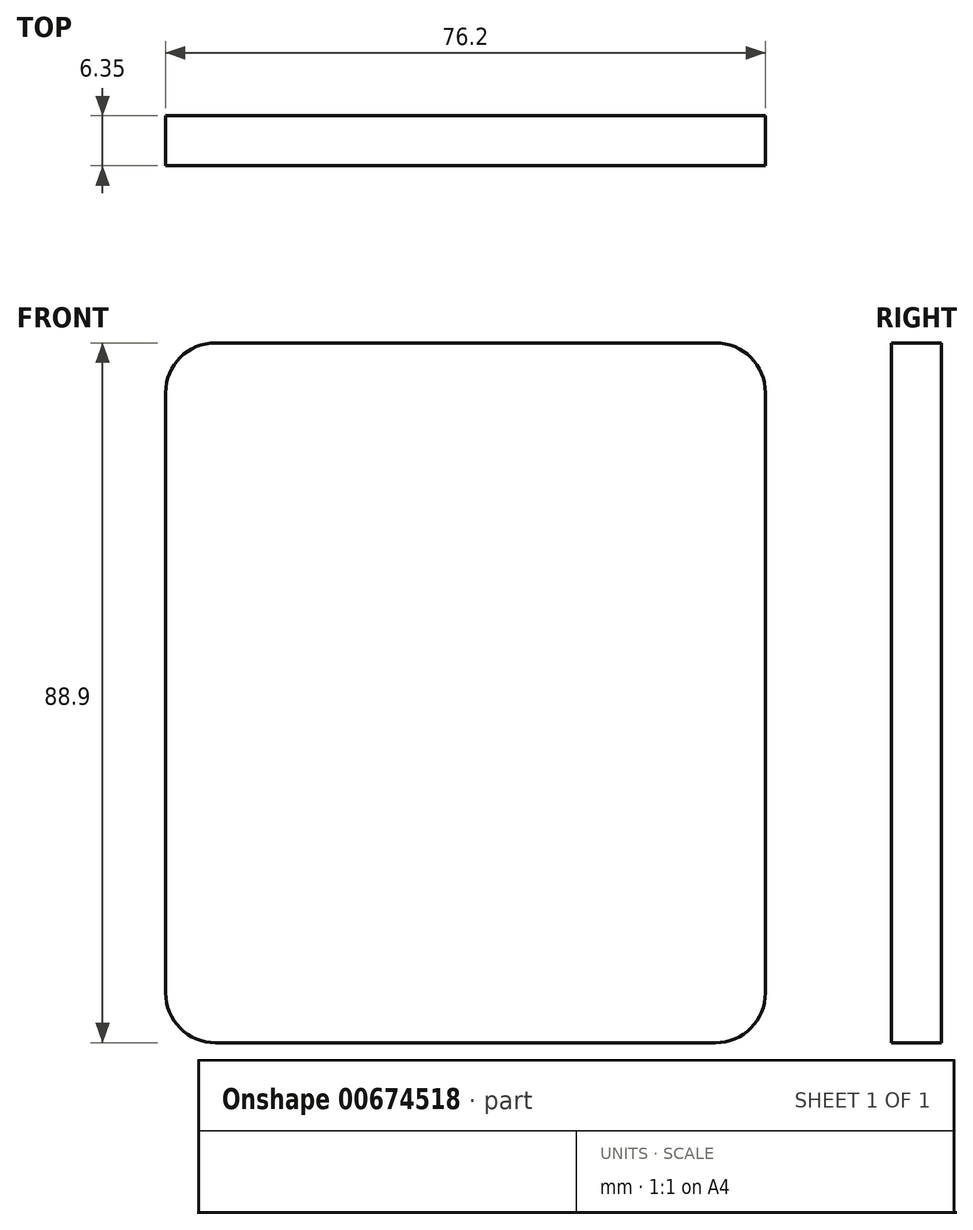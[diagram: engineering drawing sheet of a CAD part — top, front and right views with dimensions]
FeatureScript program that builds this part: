
annotation { "Feature Type Name" : "Feature", "Feature Type Description" : "" }
export const myFeature = defineFeature(function(context is Context, id is Id, definition is map)
    precondition{}
    {
        {
            var Q0;
            Q0=qCreatedBy(makeId("Front.planeOp"),FACE);
            var sketch = newSketch(context, id + "F0", { "sketchPlane" : qUnion([Q0])});
            skLineSegment(sketch, "E0.bottom", {"start": v(31.75, 44.45) * mm, "end": v(-31.75, 44.45) * mm});
            skLineSegment(sketch, "E0.top", {"start": v(31.75, -44.45) * mm, "end": v(-31.75, -44.45) * mm});
            skLineSegment(sketch, "E0.left", {"start": v(38.1, 38.1) * mm, "end": v(38.1, -38.1) * mm});
            skLineSegment(sketch, "E0.right", {"start": v(-38.1, 38.1) * mm, "end": v(-38.1, -38.1) * mm});
            skPoint(sketch, "E0.middle", {"position": v(0, 0) * mm});
            skPoint(sketch, "E1.visualSharp", {"position": v(38.1, 44.45) * mm});
            skArc(sketch, "E1.filletArc", {"start": v(38.1, 38.1) * mm, "mid": v(36.24, 42.6) * mm, "end": v(31.75, 44.45) * mm});
            skPoint(sketch, "E2.visualSharp", {"position": v(38.1, -44.45) * mm});
            skArc(sketch, "E2.filletArc", {"start": v(31.75, -44.45) * mm, "mid": v(36.24, -42.6) * mm, "end": v(38.1, -38.1) * mm});
            skPoint(sketch, "E3.visualSharp", {"position": v(-38.1, -44.45) * mm});
            skArc(sketch, "E3.filletArc", {"start": v(-38.1, -38.1) * mm, "mid": v(-36.24, -42.6) * mm, "end": v(-31.75, -44.45) * mm});
            skPoint(sketch, "E4.visualSharp", {"position": v(-38.1, 44.45) * mm});
            skArc(sketch, "E4.filletArc", {"start": v(-31.75, 44.45) * mm, "mid": v(-36.24, 42.6) * mm, "end": v(-38.1, 38.1) * mm});
            skSolve(sketch);
        }
        {
            var Q0;
            Q0 = qSketchRegion(id + "F0", true);
            extrude(context, id + "F1", {"entities" : qUnion([Q0]), "depth" : 6.35 * mm, "offsetDistance" : 25.4 * mm});
        }
    });
